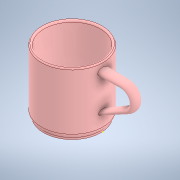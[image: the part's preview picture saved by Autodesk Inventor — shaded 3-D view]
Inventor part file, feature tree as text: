
AUTODESK INVENTOR PART (.ipt)
format: ipt  version: 2022 (Build 260153000, 153)  size: 248,320 bytes
history: native  units: mm
features: sketch x7, other x4, plane x2, revolve x1, shell x1, loft x1, fillet x1, extrude x1
ambient origin geometry x8: Origin, YZ Plane, XZ Plane, XY Plane, X Axis, Y Axis, Z Axis, Center Point
bodies: Body1 (feature_tree)
feature tree (18):
  other  "Sección transversal1"
  other  "Sección transversal2"
  other  "Sección transversal3"
  other  "Sólido1"
  revolve  "Revolución1"  [1 undecoded]
  shell  "Vaciado1"  Thickness=65.0mm
  sketch  "Boceto3"  dims[d3=32.5mm d4=90.0deg d5=3.0mm]
  sketch  "Boceto6"  dims[d6=0.5mm d7=2.0mm d8=0.0mm d9=20.0mm d13=0.5mm d14=2.0mm d15=0.0mm d16=20.0mm d26=0.5mm d27=2.0mm d28=0.0mm d29=20.0mm d38=6.0mm]
  plane  "Plano de trabajo3"
  sketch  "Boceto7"  dims[d39=4.0mm]
  sketch  "Boceto8"  dims[d40=5.0mm]
  plane  "Plano de trabajo4"
  loft  "Solevación1"
  fillet  "Empalme1"  Radius=3.0mm
  extrude  "Extrusión1"  Depth=2.0mm
  sketch  "Boceto1"  dims[d0=70.0mm d1=35.0mm d2=65.0mm]
  sketch  "Boceto9"  dims[d41=3.0mm]
  sketch  "Boceto10"  dims[d42=0.0mm d43=90.0deg d44=0.0mm d45=90.0deg d46=0.0mm d47=90.0deg d48=2.0mm d49=65.0mm d50=62.0mm d51=2.0mm d52=0.0mm]
note: 1 required parameter value undecoded (feature->parameter linkage not recoverable at this tier; creation-order binding heuristic only, values carry confidence <= 0.55)
